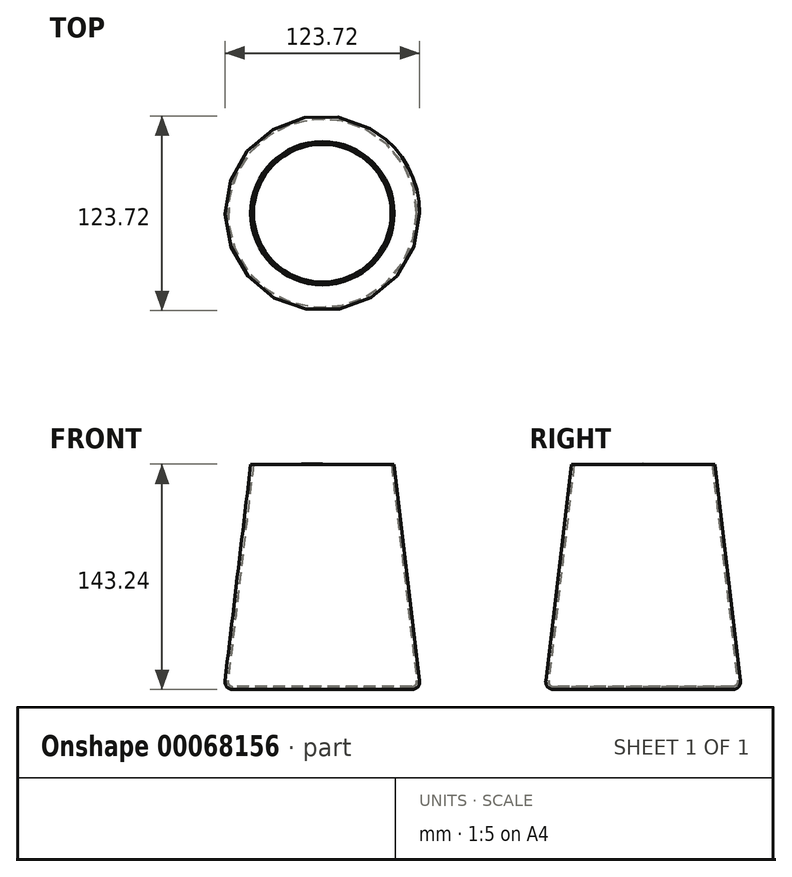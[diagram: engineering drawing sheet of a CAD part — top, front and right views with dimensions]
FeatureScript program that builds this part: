
annotation { "Feature Type Name" : "Feature", "Feature Type Description" : "" }
export const myFeature = defineFeature(function(context is Context, id is Id, definition is map)
    precondition{}
    {
        {
            var Q0;
            Q0=qCreatedBy(makeId("Top.planeOp"),FACE);
            var sketch = newSketch(context, id + "F0", { "sketchPlane" : qUnion([Q0])});
            skCircle(sketch, "E0", {"center": v(0, 0) * mm, "radius": 62.5 * mm});
            skSolve(sketch);
        }
        {
            var Q0;
            Q0=qCreatedBy(makeId("Top.planeOp"),FACE);
            cPlane(context, id + "F1", {"entities" : qUnion([Q0]), "cplaneType" : CPlaneType.OFFSET, "offset" : 143 * mm, "width" : 152.4 * mm, "height" : 152.4 * mm});
        }
        {
            var Q0;
            Q0=qCreatedBy(id+"F1.planeOp",FACE);
            var sketch = newSketch(context, id + "F2", { "sketchPlane" : qUnion([Q0])});
            skCircle(sketch, "E1", {"center": v(0, 0) * mm, "radius": 45.5 * mm});
            skSolve(sketch);
        }
        {
            var Q0;
            Q0=makeQuery(id+"F0.imprint","IMPRINT",FACE,{"disambiguationData":[TD([[makeQuery(id+"F0.imprint","IMPRINT",EDGE,{"derivedFrom":sQuery(id+"F0.wireOp",EDGE,"E0")}),1.0]])]});
            var Q1;
            Q1=makeQuery(id+"F2.imprint","IMPRINT",FACE,{"disambiguationData":[TD([[makeQuery(id+"F2.imprint","IMPRINT",EDGE,{"derivedFrom":sQuery(id+"F2.wireOp",EDGE,"E1")}),1.0]])]});
            loft(context, id + "F3", {"sheetProfilesArray" : [{ "sheetProfileEntities" : qUnion([Q0]) }, { "sheetProfileEntities" : qUnion([Q1]) }]});
        }
        {
            var Q0;
            Q0=makeQuery(id+"F3.opLoft","MID_CAP_EDGE",EDGE,{"disambiguationData":[OSD([sQuery(id+"F0.wireOp",EDGE,"E0")])],"capPos":0.0});
            fillet(context, id + "F4", {"entities" : qUnion([Q0]), "radius" : 5.08 * mm, "tangentPropagation" : true, "allowEdgeOverflow" : false});
        }
        {
            var Q0;
            Q0=makeQuery(id+"F3.opLoft","CAP_FACE",FACE,{"disambiguationData":[OSD([makeQuery(id+"F2.imprint","IMPRINT",FACE,{"disambiguationData":[TD([[makeQuery(id+"F2.imprint","IMPRINT",EDGE,{"derivedFrom":sQuery(id+"F2.wireOp",EDGE,"E1")}),1.0]])]})])],"isStart":true});
            shell(context, id + "F5", {"entities" : qUnion([Q0]), "thickness" : 1.7 * mm});
        }
        {
            var Q0;
            Q0=qCreatedBy(makeId("Front.planeOp"),FACE);
            var sketch = newSketch(context, id + "F6", { "sketchPlane" : qUnion([Q0])});
            skLineSegment(sketch, "E2", {"start": v(43.76, 143.09) * mm, "end": v(60.26, 2.08) * mm});
            skLineSegment(sketch, "E3", {"start": v(60.26, 2.08) * mm, "end": v(0, 2.08) * mm});
            skLineSegment(sketch, "E4", {"start": v(0, 2.08) * mm, "end": v(0, 143.24) * mm});
            skLineSegment(sketch, "E5", {"start": v(0, 143.24) * mm, "end": v(43.76, 143.09) * mm});
            skSolve(sketch);
        }
        {
            var Q0;
            Q0 = qSketchRegion(id + "F6", true);
            var Q1;
            Q1=sQuery(id+"F6.wireOp",EDGE,"E4");
            revolve(context, id + "F7", {"entities" : qUnion([Q0]), "axis" : qUnion([Q1]), "revolveType" : RevolveType.FULL});
        }
        {
            var Q0;
            Q0=makeQuery(id+"F7.opRevolve","SWEPT_EDGE",EDGE,{"disambiguationData":[OSD([sQuery(id+"F6.wireOp",EDGE,"E2"),sQuery(id+"F6.wireOp",EDGE,"E3")])]});
            fillet(context, id + "F8", {"entities" : qUnion([Q0]), "radius" : 3 * mm, "tangentPropagation" : true, "allowEdgeOverflow" : false});
        }
    });
